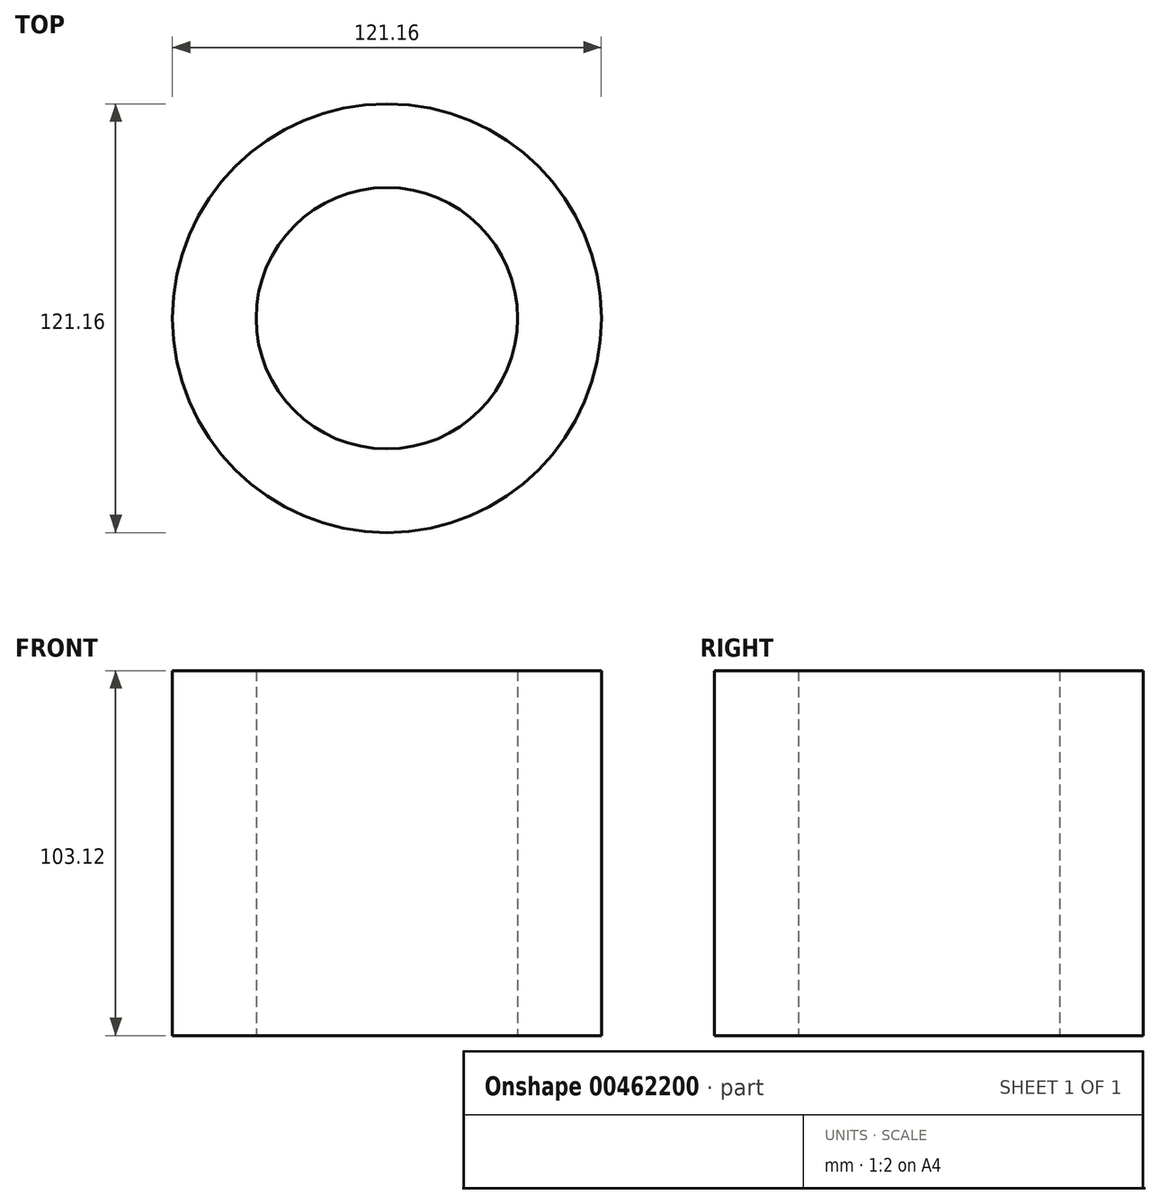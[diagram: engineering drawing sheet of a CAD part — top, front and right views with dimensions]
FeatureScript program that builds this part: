
annotation { "Feature Type Name" : "Feature", "Feature Type Description" : "" }
export const myFeature = defineFeature(function(context is Context, id is Id, definition is map)
    precondition{}
    {
        {
            var Q0;
            Q0=qCreatedBy(makeId("Top.planeOp"),FACE);
            var sketch = newSketch(context, id + "F0", { "sketchPlane" : qUnion([Q0])});
            skCircle(sketch, "E0", {"center": v(0, 0) * mm, "radius": 60.58 * mm});
            skCircle(sketch, "E1", {"center": v(0, 0) * mm, "radius": 36.94 * mm});
            skSolve(sketch);
        }
        {
            var Q0;
            Q0 = qSketchRegion(id + "F0", true);
            extrude(context, id + "F1", {"entities" : qUnion([Q0]), "depth" : 103.12 * mm});
        }
    });
